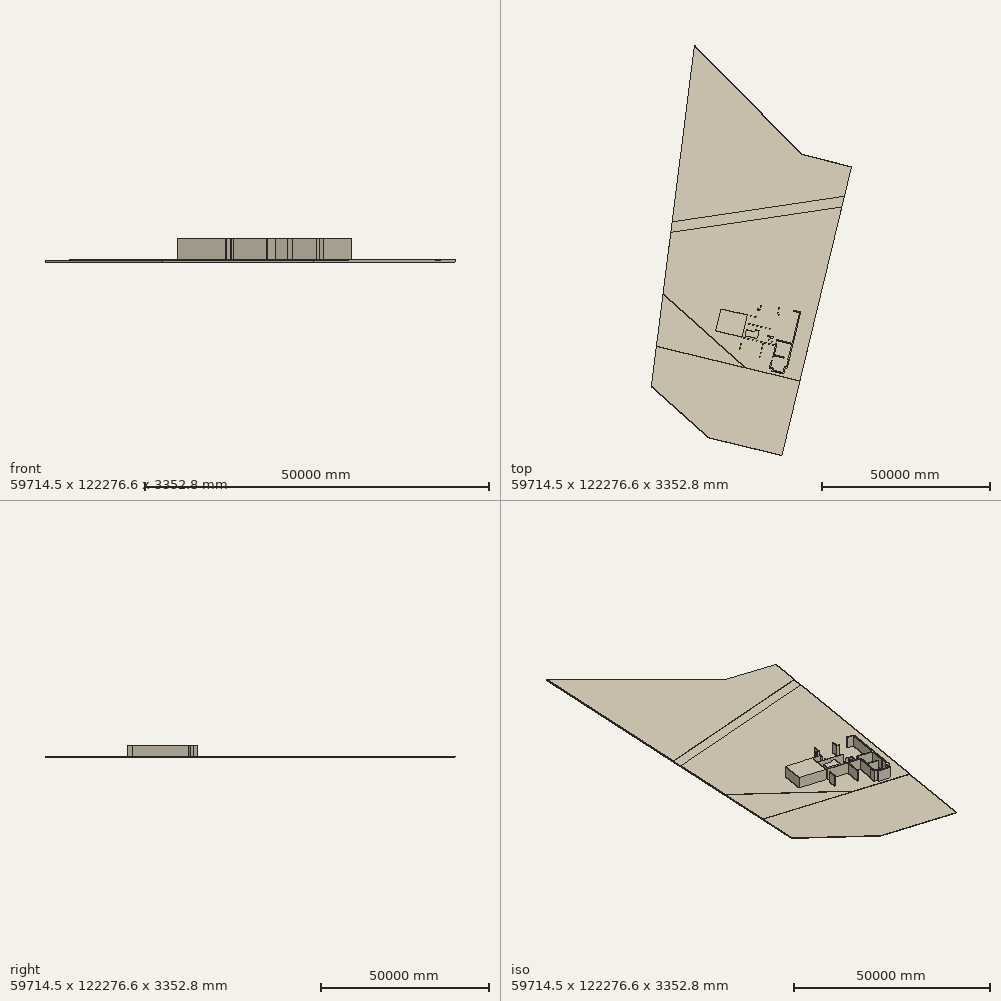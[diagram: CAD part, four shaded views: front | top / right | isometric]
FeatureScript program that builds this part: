
annotation { "Feature Type Name" : "Feature", "Feature Type Description" : "" }
export const myFeature = defineFeature(function(context is Context, id is Id, definition is map)
    precondition{}
    {
        {
            var Q0;
            Q0=qCreatedBy(makeId("Top.planeOp"),FACE);
            var sketch = newSketch(context, id + "F0", { "sketchPlane" : qUnion([Q0])});
            skLineSegment(sketch, "E0", {"start": v(0, 0) * mm, "end": v(31989.83, -32467.96) * mm});
            skLineSegment(sketch, "E1", {"start": v(31989.83, -32467.96) * mm, "end": v(46862.18, -36229.17) * mm});
            skLineSegment(sketch, "E2", {"start": v(46862.18, -36229.17) * mm, "end": v(26112.23, -122276.56) * mm});
            skLineSegment(sketch, "E3", {"start": v(46862.18, -36229.17) * mm, "end": v(46862.18, -51469.17) * mm, "construction": true});
            skLineSegment(sketch, "E4", {"start": v(0, 0) * mm, "end": v(-12852.3, -101676.89) * mm});
            skLineSegment(sketch, "E5", {"start": v(0, 0) * mm, "end": v(0, 15240) * mm, "construction": true});
            skLineSegment(sketch, "E6", {"start": v(26112.23, -122276.56) * mm, "end": v(4230, -116999.76) * mm});
            skLineSegment(sketch, "E7", {"start": v(26112.23, -122276.56) * mm, "end": v(10872.23, -122276.56) * mm, "construction": true});
            skLineSegment(sketch, "E8", {"start": v(4230, -116999.76) * mm, "end": v(-12852.3, -101676.89) * mm});
            skArc(sketch, "E9", {"start": v(-4165.07, -109469.35) * mm, "mid": v(-689.73, -114039.67) * mm, "end": v(4230, -116999.76) * mm, "construction": true});
            skArc(sketch, "E10", {"start": v(-4165.07, -109469.35) * mm, "mid": v(-8132.26, -105153.47) * mm, "end": v(-12852.3, -101676.89) * mm, "construction": true});
            skLineSegment(sketch, "E11", {"start": v(31471.2, -100053.58) * mm, "end": v(-11342.08, -89729.35) * mm});
            skLineSegment(sketch, "E12", {"start": v(-9365.85, -74095.03) * mm, "end": v(15198.72, -96129.54) * mm});
            skLineSegment(sketch, "E13", {"start": v(-6651.63, -52622.31) * mm, "end": v(44754.67, -44968.73) * mm});
            skLineSegment(sketch, "E14", {"start": v(-7048.63, -55763.02) * mm, "end": v(43983.88, -48165.09) * mm});
            skSolve(sketch);
        }
        {
            var Q0;
            {var subQ4=sQuery(id+"F0.wireOp",EDGE,"E0");Q0=makeQuery(id+"F0.imprint","IMPRINT",FACE,{"disambiguationData":[TD([[makeQuery(id+"F0.imprint","IMPRINT",EDGE,{"derivedFrom":subQ4}),-1.0]])]});}
            var Q1;
            {var subQ0=sQuery(id+"F0.wireOp",EDGE,"E13");Q1=makeQuery(id+"F0.imprint","IMPRINT",FACE,{"disambiguationData":[TD([[makeQuery(id+"F0.imprint","IMPRINT",EDGE,{"derivedFrom":subQ0}),-1.0]])]});}
            var Q2;
            {var subQ0=sQuery(id+"F0.wireOp",EDGE,"E12");Q2=makeQuery(id+"F0.imprint","IMPRINT",FACE,{"disambiguationData":[TD([[makeQuery(id+"F0.imprint","IMPRINT",EDGE,{"derivedFrom":subQ0}),1.0]])]});}
            var Q3;
            {var subQ3=sQuery(id+"F0.wireOp",EDGE,"E12");Q3=makeQuery(id+"F0.imprint","IMPRINT",FACE,{"disambiguationData":[TD([[makeQuery(id+"F0.imprint","IMPRINT",EDGE,{"derivedFrom":subQ3}),-1.0]])]});}
            var Q4;
            {var subQ1=sQuery(id+"F0.wireOp",EDGE,"E6");Q4=makeQuery(id+"F0.imprint","IMPRINT",FACE,{"disambiguationData":[TD([[makeQuery(id+"F0.imprint","IMPRINT",EDGE,{"derivedFrom":subQ1}),-1.0]])]});}
            extrude(context, id + "F1", {"entities" : qUnion([Q0, Q1, Q2, Q3, Q4]), "depth" : 304.8 * mm, "offsetDistance" : 25.4 * mm});
        }
        {
            var Q0;
            Q0=makeQuery(id+"F1.opExtrude","CAP_FACE",FACE,{"disambiguationData":[OSD([sQuery(id+"F0.wireOp",EDGE,"E0"),sQuery(id+"F0.wireOp",EDGE,"E1"),sQuery(id+"F0.wireOp",EDGE,"E2"),sQuery(id+"F0.wireOp",EDGE,"E4"),sQuery(id+"F0.wireOp",EDGE,"E6"),sQuery(id+"F0.wireOp",EDGE,"E8")])],"isStart":false});
            var sketch = newSketch(context, id + "F2", { "sketchPlane" : qUnion([Q0])});
            skLineSegment(sketch, "E15.0", {"start": v(-9365.85, -74095.03) * mm, "end": v(15198.72, -96129.54) * mm});
            skLineSegment(sketch, "E16.0", {"start": v(31471.2, -100053.58) * mm, "end": v(-11342.08, -89729.35) * mm});
            skLineSegment(sketch, "E17.0", {"start": v(0, 0) * mm, "end": v(-12852.3, -101676.89) * mm});
            skSolve(sketch);
        }
        {
            var Q0;
            {var subQ0=sQuery(id+"F2.wireOp",EDGE,"E15.0");Q0=makeQuery(id+"F2.imprint","IMPRINT",FACE,{"disambiguationData":[TD([[makeQuery(id+"F2.imprint","IMPRINT",EDGE,{"derivedFrom":subQ0}),-1.0]])]});}
            extrude(context, id + "F3", {"entities" : qUnion([Q0]), "operationType" : NewBodyOperationType.REMOVE, "oppositeDirection" : true, "depth" : 76.2 * mm, "offsetDistance" : 25.4 * mm});
        }
        {
            var Q0;
            Q0=makeQuery(id+"F1.opExtrude","CAP_FACE",FACE,{"disambiguationData":[OSD([sQuery(id+"F0.wireOp",EDGE,"E0"),sQuery(id+"F0.wireOp",EDGE,"E1"),sQuery(id+"F0.wireOp",EDGE,"E2"),sQuery(id+"F0.wireOp",EDGE,"E4"),sQuery(id+"F0.wireOp",EDGE,"E6"),sQuery(id+"F0.wireOp",EDGE,"E8")])],"isStart":false});
            var sketch = newSketch(context, id + "F4", { "sketchPlane" : qUnion([Q0])});
            skLineSegment(sketch, "E18.0", {"start": v(0, 0) * mm, "end": v(-12852.3, -101676.89) * mm});
            skLineSegment(sketch, "E19.0", {"start": v(4230, -116999.76) * mm, "end": v(-12852.3, -101676.89) * mm});
            skLineSegment(sketch, "E20.0", {"start": v(26112.23, -122276.56) * mm, "end": v(4230, -116999.76) * mm});
            skLineSegment(sketch, "E21.0", {"start": v(46862.18, -36229.17) * mm, "end": v(26112.23, -122276.56) * mm});
            skLineSegment(sketch, "E22.0", {"start": v(31471.2, -100053.58) * mm, "end": v(-11342.08, -89729.35) * mm});
            skSolve(sketch);
        }
        {
            var Q0;
            {var subQ4=sQuery(id+"F4.wireOp",EDGE,"E19.0");Q0=makeQuery(id+"F4.imprint","IMPRINT",FACE,{"disambiguationData":[TD([[makeQuery(id+"F4.imprint","IMPRINT",EDGE,{"derivedFrom":subQ4}),-1.0]])]});}
            extrude(context, id + "F5", {"entities" : qUnion([Q0]), "operationType" : NewBodyOperationType.REMOVE, "oppositeDirection" : true, "depth" : 152.4 * mm, "offsetDistance" : 25.4 * mm});
        }
        {
            var Q0;
            Q0=makeQuery(id+"F1.opExtrude","CAP_FACE",FACE,{"disambiguationData":[OSD([sQuery(id+"F0.wireOp",EDGE,"E0"),sQuery(id+"F0.wireOp",EDGE,"E1"),sQuery(id+"F0.wireOp",EDGE,"E2"),sQuery(id+"F0.wireOp",EDGE,"E4"),sQuery(id+"F0.wireOp",EDGE,"E6"),sQuery(id+"F0.wireOp",EDGE,"E8")])],"isStart":false});
            var sketch = newSketch(context, id + "F6", { "sketchPlane" : qUnion([Q0])});
            skLineSegment(sketch, "E23.0", {"start": v(-6651.63, -52622.31) * mm, "end": v(44754.67, -44968.73) * mm});
            skLineSegment(sketch, "E24.0", {"start": v(-7048.63, -55763.02) * mm, "end": v(43983.88, -48165.09) * mm});
            skLineSegment(sketch, "E25.0", {"start": v(0, 0) * mm, "end": v(-12852.3, -101676.89) * mm});
            skLineSegment(sketch, "E26.0", {"start": v(46862.18, -36229.17) * mm, "end": v(26112.23, -122276.56) * mm});
            skSolve(sketch);
        }
        {
            var Q0;
            {var subQ0=sQuery(id+"F6.wireOp",EDGE,"E23.0");Q0=makeQuery(id+"F6.imprint","IMPRINT",FACE,{"disambiguationData":[TD([[makeQuery(id+"F6.imprint","IMPRINT",EDGE,{"derivedFrom":subQ0}),-1.0]])]});}
            extrude(context, id + "F7", {"entities" : qUnion([Q0]), "operationType" : NewBodyOperationType.REMOVE, "oppositeDirection" : true, "depth" : 152.4 * mm, "offsetDistance" : 25.4 * mm});
        }
        {
            var Q0;
            {var subQ0=sQuery(id+"F0.wireOp",EDGE,"E4");var subQ1=sQuery(id+"F0.wireOp",EDGE,"E2");Q0=makeQuery(id+"F7.boolean.opBoolean","SPLIT",FACE,{"disambiguationData":[TD([makeQuery(id+"F3.boolean.opBoolean","COPY",FACE,{"derivedFrom":makeQuery(id+"F3.opExtrude","SWEPT_FACE",FACE,{"disambiguationData":[OSD([sQuery(id+"F2.wireOp",EDGE,"E15.0")])]})})])],"derivedFrom":makeQuery(id+"F1.opExtrude","CAP_FACE",FACE,{"disambiguationData":[OSD([sQuery(id+"F0.wireOp",EDGE,"E0"),sQuery(id+"F0.wireOp",EDGE,"E1"),subQ1,subQ0,sQuery(id+"F0.wireOp",EDGE,"E6"),sQuery(id+"F0.wireOp",EDGE,"E8")])],"isStart":false})});}
            var sketch = newSketch(context, id + "F8", { "sketchPlane" : qUnion([Q0])});
            skLineSegment(sketch, "E27", {"start": v(27669.68, -96315.03) * mm, "end": v(31724.64, -79499.64) * mm});
            skPoint(sketch, "E28.orphan", {"position": v(31471.2, -100053.58) * mm});
            skLineSegment(sketch, "E29", {"start": v(-5717.12, -79311.3) * mm, "end": v(3764.68, -81597.8) * mm});
            skLineSegment(sketch, "E30", {"start": v(3764.68, -81597.8) * mm, "end": v(7766.05, -65004.64) * mm});
            skLineSegment(sketch, "E31", {"start": v(7766.05, -65004.64) * mm, "end": v(-1715.76, -62718.14) * mm});
            skLineSegment(sketch, "E32", {"start": v(-1715.76, -62718.14) * mm, "end": v(-5717.12, -79311.3) * mm});
            skLineSegment(sketch, "E33", {"start": v(-5145.5, -76940.85) * mm, "end": v(-2182.44, -77655.38) * mm});
            skLineSegment(sketch, "E34", {"start": v(-2182.44, -77655.38) * mm, "end": v(-2754.06, -80025.83) * mm});
            skLineSegment(sketch, "E35", {"start": v(-5145.5, -76940.85) * mm, "end": v(-9590.1, -75869.05) * mm});
            skLineSegment(sketch, "E36", {"start": v(-2182.44, -77655.38) * mm, "end": v(1247.3, -63432.67) * mm});
            skLineSegment(sketch, "E37", {"start": v(3764.68, -81597.8) * mm, "end": v(7190.64, -82423.95) * mm});
            skLineSegment(sketch, "E38", {"start": v(4934.3, -91780.7) * mm, "end": v(-10343.91, -88096.42) * mm});
            skLineSegment(sketch, "E39.0", {"start": v(4230, -116999.76) * mm, "end": v(-12852.3, -101676.89) * mm});
            skLineSegment(sketch, "E40", {"start": v(-2047.33, -90097.1) * mm, "end": v(-6264.7, -107585.98) * mm});
            skLineSegment(sketch, "E41", {"start": v(-5603, -89239.67) * mm, "end": v(-9358.03, -104811.25) * mm});
            skArc(sketch, "E42", {"start": v(-6746.26, -93980.57) * mm, "mid": v(-7326.44, -90293.4) * mm, "end": v(-10343.91, -88096.42) * mm});
            skLineSegment(sketch, "E43", {"start": v(-8087.58, -78739.68) * mm, "end": v(-10343.91, -88096.42) * mm});
            skLineSegment(sketch, "E44", {"start": v(-5717.12, -79311.3) * mm, "end": v(-8087.58, -78739.68) * mm});
            skLineSegment(sketch, "E45", {"start": v(22775.38, -94507.71) * mm, "end": v(22346.66, -96285.55) * mm});
            skLineSegment(sketch, "E46", {"start": v(22346.66, -96285.55) * mm, "end": v(23235.58, -96499.91) * mm});
            skLineSegment(sketch, "E47", {"start": v(23235.58, -96499.91) * mm, "end": v(23092.67, -97092.52) * mm});
            skLineSegment(sketch, "E48", {"start": v(23092.67, -97092.52) * mm, "end": v(26648.35, -97949.96) * mm});
            skLineSegment(sketch, "E49", {"start": v(26648.35, -97949.96) * mm, "end": v(27077.07, -96172.12) * mm});
            skLineSegment(sketch, "E50", {"start": v(13071.34, -92167.63) * mm, "end": v(14241.39, -87315.61) * mm});
            skLineSegment(sketch, "E51", {"start": v(14241.39, -87315.61) * mm, "end": v(5985.04, -85324.63) * mm});
            skLineSegment(sketch, "E52", {"start": v(5985.04, -85324.63) * mm, "end": v(7699.91, -78213.28) * mm});
            skLineSegment(sketch, "E53", {"start": v(14020.33, -75230.32) * mm, "end": v(31724.64, -79499.64) * mm});
            skLineSegment(sketch, "E54.trimOffspring", {"start": v(27077.07, -96172.12) * mm, "end": v(27669.68, -96315.03) * mm});
            skLineSegment(sketch, "E55.0", {"start": v(6352.8, -85099.78) * mm, "end": v(7924.77, -78581.03) * mm});
            skLineSegment(sketch, "E55.1", {"start": v(23460.43, -96867.67) * mm, "end": v(26423.5, -97582.2) * mm});
            skLineSegment(sketch, "E55.2", {"start": v(26423.5, -97582.2) * mm, "end": v(26852.22, -95804.36) * mm});
            skLineSegment(sketch, "E55.3", {"start": v(26852.22, -95804.36) * mm, "end": v(27444.83, -95947.27) * mm});
            skLineSegment(sketch, "E55.4", {"start": v(27444.83, -95947.27) * mm, "end": v(28016.45, -93576.82) * mm});
            skLineSegment(sketch, "E55.5", {"start": v(23603.34, -96275.06) * mm, "end": v(23460.43, -96867.67) * mm});
            skLineSegment(sketch, "E55.6", {"start": v(14245.18, -75598.08) * mm, "end": v(19282.4, -76812.78) * mm});
            skLineSegment(sketch, "E55.7", {"start": v(22714.42, -96060.7) * mm, "end": v(23603.34, -96275.06) * mm});
            skLineSegment(sketch, "E55.8", {"start": v(23143.14, -94282.86) * mm, "end": v(22714.42, -96060.7) * mm});
            skLineSegment(sketch, "E55.9", {"start": v(13439.1, -91942.77) * mm, "end": v(23143.14, -94282.86) * mm});
            skLineSegment(sketch, "E55.10", {"start": v(13439.1, -91942.77) * mm, "end": v(14609.14, -87090.76) * mm});
            skLineSegment(sketch, "E55.11", {"start": v(14609.14, -87090.76) * mm, "end": v(6352.8, -85099.78) * mm});
            skLineSegment(sketch, "E56", {"start": v(14609.14, -87090.76) * mm, "end": v(19350.05, -88234) * mm});
            skLineSegment(sketch, "E57", {"start": v(20619.6, -88657.73) * mm, "end": v(19476.35, -93398.63) * mm});
            skLineSegment(sketch, "E58.0", {"start": v(20508.48, -88630.93) * mm, "end": v(19365.23, -93371.83) * mm});
            skLineSegment(sketch, "E58.1", {"start": v(14582.35, -87201.87) * mm, "end": v(20508.48, -88630.93) * mm});
            skLineSegment(sketch, "E59", {"start": v(17710.43, -83331.52) * mm, "end": v(18255.26, -81072.19) * mm});
            skLineSegment(sketch, "E60", {"start": v(17821.54, -83358.32) * mm, "end": v(19393.5, -76839.58) * mm});
            skLineSegment(sketch, "E61", {"start": v(7924.77, -78581.03) * mm, "end": v(18255.26, -81072.19) * mm});
            skLineSegment(sketch, "E62", {"start": v(14020.33, -75230.32) * mm, "end": v(12993.2, -79489.73) * mm});
            skLineSegment(sketch, "E63", {"start": v(12993.2, -79489.73) * mm, "end": v(7699.91, -78213.28) * mm});
            skLineSegment(sketch, "E64", {"start": v(14245.18, -75598.08) * mm, "end": v(13218.05, -79857.49) * mm});
            skLineSegment(sketch, "E65", {"start": v(13244.84, -79746.37) * mm, "end": v(18282.05, -80961.07) * mm});
            skLineSegment(sketch, "E66", {"start": v(23143.14, -94282.86) * mm, "end": v(23571.86, -92505.02) * mm});
            skLineSegment(sketch, "E67", {"start": v(24202.07, -89404.05) * mm, "end": v(19350.05, -88234) * mm});
            skLineSegment(sketch, "E68", {"start": v(23032.02, -94256.07) * mm, "end": v(24175.27, -89515.16) * mm});
            skLineSegment(sketch, "E69", {"start": v(24175.27, -89515.16) * mm, "end": v(20619.6, -88657.73) * mm});
            skLineSegment(sketch, "E70", {"start": v(19833.61, -91917.1) * mm, "end": v(21018.84, -92202.9) * mm});
            skLineSegment(sketch, "E71", {"start": v(21018.84, -92202.9) * mm, "end": v(21519, -90128.76) * mm});
            skLineSegment(sketch, "E72", {"start": v(21519, -90128.76) * mm, "end": v(23889.46, -90700.39) * mm});
            skLineSegment(sketch, "E73", {"start": v(23571.86, -92505.02) * mm, "end": v(28016.45, -93576.82) * mm});
            skLineSegment(sketch, "E74", {"start": v(23828.5, -92253.37) * mm, "end": v(27982.96, -93255.2) * mm});
            skLineSegment(sketch, "E75.trimOffspring", {"start": v(18282.05, -80961.07) * mm, "end": v(19282.4, -76812.78) * mm});
            skLineSegment(sketch, "E76", {"start": v(28983.3, -89106.91) * mm, "end": v(24828.84, -88105.08) * mm});
            skLineSegment(sketch, "E77", {"start": v(27982.96, -93255.2) * mm, "end": v(28983.3, -89106.91) * mm});
            skLineSegment(sketch, "E78", {"start": v(23828.5, -92253.37) * mm, "end": v(24828.84, -88105.08) * mm});
            skLineSegment(sketch, "E79.trimOffspring", {"start": v(29159.7, -88835.91) * mm, "end": v(31356.88, -79724.5) * mm});
            skLineSegment(sketch, "E80", {"start": v(29159.7, -88835.91) * mm, "end": v(24603.99, -87737.32) * mm});
            skLineSegment(sketch, "E81", {"start": v(24603.99, -87737.32) * mm, "end": v(24202.07, -89404.05) * mm});
            skLineSegment(sketch, "E82", {"start": v(26023.36, -78438.34) * mm, "end": v(24951.57, -82882.93) * mm});
            skLineSegment(sketch, "E83", {"start": v(24951.57, -82882.93) * mm, "end": v(30285.09, -84169.09) * mm});
            skLineSegment(sketch, "E84", {"start": v(25912.25, -78411.54) * mm, "end": v(24340.28, -84930.28) * mm});
            skLineSegment(sketch, "E85", {"start": v(24924.77, -82994.05) * mm, "end": v(30258.3, -84280.2) * mm});
            skLineSegment(sketch, "E86", {"start": v(21057.5, -78390.48) * mm, "end": v(23724.26, -79033.55) * mm});
            skLineSegment(sketch, "E87", {"start": v(23724.26, -79033.55) * mm, "end": v(23474.18, -80070.63) * mm});
            skLineSegment(sketch, "E88", {"start": v(23474.18, -80070.63) * mm, "end": v(20807.42, -79427.55) * mm});
            skLineSegment(sketch, "E89", {"start": v(20807.42, -79427.55) * mm, "end": v(21057.5, -78390.48) * mm});
            skLineSegment(sketch, "E90", {"start": v(12993.2, -79489.73) * mm, "end": v(12921.74, -79786.03) * mm});
            skLineSegment(sketch, "E91", {"start": v(17821.54, -83358.32) * mm, "end": v(24340.28, -84930.28) * mm});
            skLineSegment(sketch, "E92", {"start": v(25961.85, -83244.13) * mm, "end": v(25553.97, -84935.55) * mm});
            skLineSegment(sketch, "E93", {"start": v(15313.18, -82871.01) * mm, "end": v(24424.6, -85068.2) * mm});
            skLineSegment(sketch, "E94", {"start": v(24424.6, -85068.2) * mm, "end": v(24924.77, -82994.05) * mm});
            skLineSegment(sketch, "E95", {"start": v(25054.81, -81967.22) * mm, "end": v(24462.2, -81824.31) * mm});
            skLineSegment(sketch, "E96", {"start": v(24462.2, -81824.31) * mm, "end": v(23747.67, -84787.38) * mm});
            skLineSegment(sketch, "E97", {"start": v(22853.5, -83944.68) * mm, "end": v(17964.45, -82765.7) * mm});
            skLineSegment(sketch, "E98", {"start": v(18807.15, -81871.54) * mm, "end": v(19128.68, -80538.16) * mm});
            skLineSegment(sketch, "E99", {"start": v(19128.68, -80538.16) * mm, "end": v(18536.07, -80395.25) * mm});
            skLineSegment(sketch, "E100", {"start": v(20165.76, -80788.24) * mm, "end": v(19879.94, -81973.47) * mm});
            skLineSegment(sketch, "E101", {"start": v(19879.94, -81973.47) * mm, "end": v(23139.32, -82759.45) * mm});
            skLineSegment(sketch, "E102", {"start": v(23139.32, -82759.45) * mm, "end": v(23425.13, -81574.23) * mm});
            skLineSegment(sketch, "E103", {"start": v(23425.13, -81574.23) * mm, "end": v(20165.76, -80788.24) * mm});
            skLineSegment(sketch, "E104", {"start": v(18920.13, -78802.6) * mm, "end": v(19512.74, -78945.51) * mm});
            skLineSegment(sketch, "E105", {"start": v(19512.74, -78945.51) * mm, "end": v(19986.12, -76982.48) * mm});
            skLineSegment(sketch, "E106.0", {"start": v(19597.06, -79083.42) * mm, "end": v(20097.24, -77009.28) * mm});
            skLineSegment(sketch, "E106.1", {"start": v(18893.34, -78913.72) * mm, "end": v(19597.06, -79083.42) * mm});
            skLineSegment(sketch, "E107", {"start": v(19393.5, -76839.58) * mm, "end": v(25912.25, -78411.54) * mm});
            skLineSegment(sketch, "E108.trimOffspring", {"start": v(26023.36, -78438.34) * mm, "end": v(31356.88, -79724.5) * mm});
            skLineSegment(sketch, "E109", {"start": v(27837.43, -93533.65) * mm, "end": v(27908.89, -93237.34) * mm});
            skLineSegment(sketch, "E110", {"start": v(26948.51, -93319.29) * mm, "end": v(27019.97, -93022.98) * mm});
            skLineSegment(sketch, "E111", {"start": v(26972.33, -93220.52) * mm, "end": v(27861.25, -93434.88) * mm});
            skLineSegment(sketch, "E112", {"start": v(26963.4, -93257.56) * mm, "end": v(27852.32, -93471.92) * mm});
            skLineSegment(sketch, "E113", {"start": v(24810.98, -88179.16) * mm, "end": v(24514.67, -88107.7) * mm});
            skLineSegment(sketch, "E114", {"start": v(24300.31, -88996.63) * mm, "end": v(24596.62, -89068.08) * mm});
            skLineSegment(sketch, "E115", {"start": v(24362.04, -89011.51) * mm, "end": v(24576.4, -88122.6) * mm});
            skLineSegment(sketch, "E116", {"start": v(24399.08, -89020.44) * mm, "end": v(24613.44, -88131.52) * mm});
            skLineSegment(sketch, "E117", {"start": v(23016.84, -89118.24) * mm, "end": v(23543.8, -86932.98) * mm});
            skLineSegment(sketch, "E118", {"start": v(22905.73, -89091.44) * mm, "end": v(23405.9, -87017.3) * mm});
            skLineSegment(sketch, "E119", {"start": v(15884.8, -80500.56) * mm, "end": v(14312.84, -87019.3) * mm});
            skLineSegment(sketch, "E120", {"start": v(15339.97, -82759.9) * mm, "end": v(17710.43, -83331.52) * mm});
            skLineSegment(sketch, "E121", {"start": v(18807.15, -81871.54) * mm, "end": v(18214.53, -81728.63) * mm});
            skLineSegment(sketch, "E122", {"start": v(13071.34, -92167.63) * mm, "end": v(23071.68, -94579.17) * mm});
            skLineSegment(sketch, "E123", {"start": v(19247.36, -85896.9) * mm, "end": v(23543.8, -86932.98) * mm});
            skLineSegment(sketch, "E124", {"start": v(19109.45, -85981.23) * mm, "end": v(19739.1, -86133.06) * mm});
            skLineSegment(sketch, "E125", {"start": v(22016.8, -88877.08) * mm, "end": v(22516.98, -86802.94) * mm});
            skLineSegment(sketch, "E126", {"start": v(21905.7, -88850.29) * mm, "end": v(22405.86, -86776.14) * mm});
            skLineSegment(sketch, "E127", {"start": v(20090.81, -88412.64) * mm, "end": v(20590.98, -86338.5) * mm});
            skLineSegment(sketch, "E128", {"start": v(20201.93, -88439.43) * mm, "end": v(20702.1, -86365.29) * mm});
            skLineSegment(sketch, "E129", {"start": v(20344.83, -87846.82) * mm, "end": v(22048.6, -88257.67) * mm});
            skCircle(sketch, "E130", {"center": v(20717.84, -88250.3) * mm, "radius": 152.4 * mm});
            skCircle(sketch, "E131", {"center": v(21532.68, -88446.8) * mm, "radius": 152.4 * mm});
            skLineSegment(sketch, "E132", {"start": v(19473.5, -88263.78) * mm, "end": v(19544.96, -87967.47) * mm});
            skLineSegment(sketch, "E133", {"start": v(19544.96, -87967.47) * mm, "end": v(20038.8, -88086.56) * mm});
            skLineSegment(sketch, "E134", {"start": v(20038.8, -88086.56) * mm, "end": v(19967.35, -88382.87) * mm});
            skLineSegment(sketch, "E135", {"start": v(19643.73, -87991.29) * mm, "end": v(19756.86, -87522.14) * mm});
            skLineSegment(sketch, "E136", {"start": v(19756.86, -87522.14) * mm, "end": v(20053.17, -87593.59) * mm});
            skLineSegment(sketch, "E137", {"start": v(20053.17, -87593.59) * mm, "end": v(19940.04, -88062.74) * mm});
            skLineSegment(sketch, "E138", {"start": v(19760.9, -86530.24) * mm, "end": v(20501.67, -86708.88) * mm});
            skLineSegment(sketch, "E139", {"start": v(20600.87, -86785.05) * mm, "end": v(20489.76, -86758.26) * mm});
            skLineSegment(sketch, "E140", {"start": v(20346.85, -87350.87) * mm, "end": v(20457.97, -87377.67) * mm});
            skLineSegment(sketch, "E141", {"start": v(20402.41, -87364.27) * mm, "end": v(20545.32, -86771.66) * mm});
            skArc(sketch, "E142", {"start": v(20402.41, -87364.27) * mm, "mid": v(20012.42, -87067.68) * mm, "end": v(19966.67, -86579.86) * mm, "construction": true});
            skLineSegment(sketch, "E143", {"start": v(22231.16, -87988.16) * mm, "end": v(23120.08, -88202.52) * mm});
            skLineSegment(sketch, "E144", {"start": v(23120.08, -88202.52) * mm, "end": v(22016.8, -88877.08) * mm});
            skLineSegment(sketch, "E145", {"start": v(22231.16, -87988.16) * mm, "end": v(22905.73, -89091.44) * mm});
            skCircle(sketch, "E146", {"center": v(22568.44, -88539.8) * mm, "radius": 50.8 * mm});
            skLineSegment(sketch, "E147", {"start": v(22427.66, -87173.32) * mm, "end": v(23316.58, -87387.68) * mm});
            skLineSegment(sketch, "E148", {"start": v(22304.64, -87195.9) * mm, "end": v(22415.75, -87222.7) * mm});
            skLineSegment(sketch, "E149", {"start": v(22161.73, -87788.52) * mm, "end": v(22272.85, -87815.32) * mm});
            skLineSegment(sketch, "E150", {"start": v(22360.2, -87209.3) * mm, "end": v(22217.29, -87801.92) * mm});
            skArc(sketch, "E151", {"start": v(22217.29, -87801.92) * mm, "mid": v(22699.6, -87715.68) * mm, "end": v(22962.65, -87302.33) * mm, "construction": true});
            skLineSegment(sketch, "E152", {"start": v(19461.72, -85007.99) * mm, "end": v(21239.56, -85436.7) * mm});
            skLineSegment(sketch, "E153", {"start": v(19390.27, -85304.3) * mm, "end": v(21168.1, -85733.01) * mm});
            skLineSegment(sketch, "E154", {"start": v(20612.78, -86735.67) * mm, "end": v(20909.09, -86807.12) * mm});
            skLineSegment(sketch, "E155", {"start": v(21239.56, -85436.7) * mm, "end": v(21025.2, -86325.63) * mm});
            skLineSegment(sketch, "E156", {"start": v(21980.33, -85615.34) * mm, "end": v(21765.97, -86504.26) * mm});
            skLineSegment(sketch, "E157", {"start": v(21099.28, -86343.49) * mm, "end": v(21072.48, -86454.6) * mm});
            skLineSegment(sketch, "E158", {"start": v(21691.9, -86486.4) * mm, "end": v(21665.1, -86597.5) * mm});
            skLineSegment(sketch, "E159", {"start": v(21085.88, -86399.05) * mm, "end": v(21678.5, -86541.95) * mm});
            skLineSegment(sketch, "E160", {"start": v(20909.09, -86807.12) * mm, "end": v(20998.4, -86436.74) * mm});
            skLineSegment(sketch, "E161", {"start": v(21649.86, -86985.76) * mm, "end": v(21739.17, -86615.37) * mm});
            skLineSegment(sketch, "E162.trimOffspring", {"start": v(21649.86, -86985.76) * mm, "end": v(22316.55, -87146.52) * mm});
            skLineSegment(sketch, "E163.trimOffspring", {"start": v(21908.87, -85911.64) * mm, "end": v(23686.71, -86340.36) * mm});
            skLineSegment(sketch, "E164.trimOffspring", {"start": v(21980.33, -85615.34) * mm, "end": v(23758.16, -86044.06) * mm});
            skLineSegment(sketch, "E165", {"start": v(15482.88, -82167.29) * mm, "end": v(17853.33, -82738.9) * mm});
            skLineSegment(sketch, "E166", {"start": v(15741.9, -81093.17) * mm, "end": v(18112.35, -81664.8) * mm});
            skLineSegment(sketch, "E167", {"start": v(17889.06, -82590.76) * mm, "end": v(18000.17, -82617.55) * mm});
            skLineSegment(sketch, "E168", {"start": v(18067.7, -81850) * mm, "end": v(18178.8, -81876.79) * mm});
            skLineSegment(sketch, "E169", {"start": v(18123.25, -81863.39) * mm, "end": v(17944.62, -82604.15) * mm});
            skLineSegment(sketch, "E170", {"start": v(15397.07, -82035.55) * mm, "end": v(15508.19, -82062.34) * mm});
            skLineSegment(sketch, "E171", {"start": v(15611.43, -81146.63) * mm, "end": v(15722.55, -81173.42) * mm});
            skLineSegment(sketch, "E172", {"start": v(15666.99, -81160.03) * mm, "end": v(15452.63, -82048.95) * mm});
            skLineSegment(sketch, "E173", {"start": v(22853.5, -83944.68) * mm, "end": v(22710.6, -84537.3) * mm});
            skLineSegment(sketch, "E174", {"start": v(22784.67, -84555.16) * mm, "end": v(22757.88, -84666.27) * mm});
            skLineSegment(sketch, "E175", {"start": v(23673.6, -84769.51) * mm, "end": v(23646.8, -84880.63) * mm});
            skLineSegment(sketch, "E176", {"start": v(25412.08, -80485.69) * mm, "end": v(24708.35, -80315.99) * mm});
            skLineSegment(sketch, "E177", {"start": v(24708.35, -80315.99) * mm, "end": v(25208.52, -78241.84) * mm});
            skLineSegment(sketch, "E178", {"start": v(18460.68, -80220.3) * mm, "end": v(18571.8, -80247.1) * mm});
            skLineSegment(sketch, "E179", {"start": v(18746.5, -79035.08) * mm, "end": v(18857.6, -79061.87) * mm});
            skLineSegment(sketch, "E180", {"start": v(19210.94, -77109.09) * mm, "end": v(19322.05, -77135.88) * mm});
            skLineSegment(sketch, "E181", {"start": v(18877.5, -78491.85) * mm, "end": v(18988.6, -78518.65) * mm});
            skLineSegment(sketch, "E182", {"start": v(19044.22, -77800.47) * mm, "end": v(19155.33, -77827.26) * mm});
            skLineSegment(sketch, "E183", {"start": v(18933.05, -78505.25) * mm, "end": v(19099.77, -77813.87) * mm});
            skLineSegment(sketch, "E184", {"start": v(19099.77, -77813.87) * mm, "end": v(19266.5, -77122.48) * mm});
            skLineSegment(sketch, "E185", {"start": v(25319.64, -78268.64) * mm, "end": v(24846.26, -80231.67) * mm});
            skLineSegment(sketch, "E186", {"start": v(24846.26, -80231.67) * mm, "end": v(25438.87, -80374.57) * mm});
            skLineSegment(sketch, "E187", {"start": v(26072.96, -83270.93) * mm, "end": v(25665.08, -84962.34) * mm});
            skLineSegment(sketch, "E188", {"start": v(25715.7, -84752.46) * mm, "end": v(29901.03, -85761.73) * mm});
            skLineSegment(sketch, "E189", {"start": v(25688.9, -84863.58) * mm, "end": v(29874.23, -85872.85) * mm});
            skLineSegment(sketch, "E190", {"start": v(28554.53, -83869.35) * mm, "end": v(28197.26, -85350.88) * mm});
            skLineSegment(sketch, "E191", {"start": v(28443.41, -83842.55) * mm, "end": v(28086.15, -85324.08) * mm});
            skLineSegment(sketch, "E192", {"start": v(27702.65, -83663.92) * mm, "end": v(27345.38, -85145.45) * mm});
            skLineSegment(sketch, "E193", {"start": v(25941.96, -83814.16) * mm, "end": v(26830.88, -84028.52) * mm});
            skLineSegment(sketch, "E194", {"start": v(26830.88, -84028.52) * mm, "end": v(26961.88, -83485.29) * mm});
            skLineSegment(sketch, "E195", {"start": v(27085.34, -83515.06) * mm, "end": v(27013.89, -83811.37) * mm});
            skLineSegment(sketch, "E196", {"start": v(27013.89, -83811.37) * mm, "end": v(27507.73, -83930.45) * mm});
            skLineSegment(sketch, "E197", {"start": v(27507.73, -83930.45) * mm, "end": v(27579.19, -83634.15) * mm});
            skLineSegment(sketch, "E198", {"start": v(27112.66, -83835.18) * mm, "end": v(26999.52, -84304.34) * mm});
            skLineSegment(sketch, "E199", {"start": v(26999.52, -84304.34) * mm, "end": v(27295.83, -84375.79) * mm});
            skLineSegment(sketch, "E200", {"start": v(27295.83, -84375.79) * mm, "end": v(27408.96, -83906.64) * mm});
            skLineSegment(sketch, "E201", {"start": v(25762.98, -84881.44) * mm, "end": v(25789.77, -84770.32) * mm});
            skLineSegment(sketch, "E202", {"start": v(26355.6, -85024.34) * mm, "end": v(26382.39, -84913.23) * mm});
            skLineSegment(sketch, "E203", {"start": v(25776.38, -84825.88) * mm, "end": v(26368.99, -84968.79) * mm});
            skArc(sketch, "E204", {"start": v(26368.99, -84968.79) * mm, "mid": v(26275.53, -84475.95) * mm, "end": v(25844.08, -84220.05) * mm, "construction": true});
            skLineSegment(sketch, "E205", {"start": v(28340.17, -84758.27) * mm, "end": v(30043.93, -85169.12) * mm});
            skLineSegment(sketch, "E206", {"start": v(28366.96, -84647.15) * mm, "end": v(30070.73, -85058) * mm});
            skLineSegment(sketch, "E207", {"start": v(29278.79, -88342.07) * mm, "end": v(27303.41, -87865.72) * mm});
            skLineSegment(sketch, "E208", {"start": v(27303.41, -87865.72) * mm, "end": v(27755.95, -85989.1) * mm});
            skLineSegment(sketch, "E209", {"start": v(27755.95, -85989.1) * mm, "end": v(29731.32, -86465.46) * mm});
            skLineSegment(sketch, "E210", {"start": v(28296.03, -85374.7) * mm, "end": v(28269.24, -85485.81) * mm});
            skLineSegment(sketch, "E211", {"start": v(29777.56, -85731.96) * mm, "end": v(29750.77, -85843.08) * mm});
            skLineSegment(sketch, "E212", {"start": v(29036.8, -85553.33) * mm, "end": v(29010, -85664.44) * mm});
            skLineSegment(sketch, "E213", {"start": v(28282.63, -85430.25) * mm, "end": v(29023.4, -85608.89) * mm});
            skLineSegment(sketch, "E214", {"start": v(29023.4, -85608.89) * mm, "end": v(29764.17, -85787.52) * mm});
            skArc(sketch, "E215", {"start": v(25137.16, -86664) * mm, "mid": v(24733.67, -87037.01) * mm, "end": v(24922.8, -87552.92) * mm});
            skLineSegment(sketch, "E216", {"start": v(26429.67, -85042.2) * mm, "end": v(26197.45, -86005.2) * mm});
            skLineSegment(sketch, "E217", {"start": v(26197.45, -86005.2) * mm, "end": v(25456.68, -85826.57) * mm});
            skLineSegment(sketch, "E218", {"start": v(26540.78, -85069) * mm, "end": v(26281.77, -86143.11) * mm});
            skLineSegment(sketch, "E219", {"start": v(26281.77, -86143.11) * mm, "end": v(25429.88, -85937.69) * mm});
            skLineSegment(sketch, "E220", {"start": v(26405.85, -85140.98) * mm, "end": v(26516.97, -85167.77) * mm});
            skLineSegment(sketch, "E221", {"start": v(26215.3, -85931.13) * mm, "end": v(26326.42, -85957.92) * mm});
            skLineSegment(sketch, "E222", {"start": v(26461.4, -85154.37) * mm, "end": v(26270.87, -85944.52) * mm});
            skArc(sketch, "E223", {"start": v(26270.87, -85944.52) * mm, "mid": v(26927.99, -85819.92) * mm, "end": v(27269.18, -85244.65) * mm, "construction": true});
            skLineSegment(sketch, "E224", {"start": v(25363.43, -85725.7) * mm, "end": v(25474.54, -85752.5) * mm});
            skLineSegment(sketch, "E225", {"start": v(25553.97, -84935.55) * mm, "end": v(25665.08, -84962.34) * mm});
            skLineSegment(sketch, "E226.trimOffspring", {"start": v(25363.43, -85725.7) * mm, "end": v(24863.26, -87799.85) * mm});
            skLineSegment(sketch, "E227.trimOffspring", {"start": v(25474.54, -85752.5) * mm, "end": v(24974.37, -87826.64) * mm});
            skLineSegment(sketch, "E228", {"start": v(24733.67, -87037.01) * mm, "end": v(25029.98, -87108.46) * mm, "construction": true});
            skLineSegment(sketch, "E229", {"start": v(23543.8, -86932.98) * mm, "end": v(23758.16, -86044.06) * mm});
            skLineSegment(sketch, "E230", {"start": v(20717.84, -88250.3) * mm, "end": v(21532.68, -88446.8) * mm, "construction": true});
            skLineSegment(sketch, "E231", {"start": v(14201.72, -86992.5) * mm, "end": v(15773.69, -80473.77) * mm});
            skLineSegment(sketch, "E232", {"start": v(15063.1, -83908.09) * mm, "end": v(19470.65, -84970.95) * mm});
            skLineSegment(sketch, "E233", {"start": v(19739.1, -86133.06) * mm, "end": v(19238.93, -88207.2) * mm});
            skLineSegment(sketch, "E234", {"start": v(19470.65, -84970.95) * mm, "end": v(19247.36, -85896.9) * mm});
            skLineSegment(sketch, "E235.trimOffspring", {"start": v(19850.22, -86159.86) * mm, "end": v(19350.05, -88234) * mm});
            skLineSegment(sketch, "E236.trimOffspring", {"start": v(19850.22, -86159.86) * mm, "end": v(23405.9, -87017.3) * mm});
            skLineSegment(sketch, "E237", {"start": v(15036.3, -84019.2) * mm, "end": v(19332.74, -85055.27) * mm});
            skLineSegment(sketch, "E238", {"start": v(19332.74, -85055.27) * mm, "end": v(19109.45, -85981.23) * mm});
            skLineSegment(sketch, "E239", {"start": v(23000.54, -90486.03) * mm, "end": v(23286.35, -89300.8) * mm});
            skLineSegment(sketch, "E240", {"start": v(20809.72, -93720.17) * mm, "end": v(20738.27, -94016.47) * mm});
            skLineSegment(sketch, "E241", {"start": v(21698.64, -93934.53) * mm, "end": v(21627.2, -94230.83) * mm});
            skLineSegment(sketch, "E242", {"start": v(20774, -93868.32) * mm, "end": v(21662.92, -94082.68) * mm});
            skLineSegment(sketch, "E243", {"start": v(18295.67, -84805.18) * mm, "end": v(18152.76, -85397.8) * mm});
            skLineSegment(sketch, "E244", {"start": v(18152.76, -85397.8) * mm, "end": v(15486, -84754.72) * mm});
            skLineSegment(sketch, "E245", {"start": v(15486, -84754.72) * mm, "end": v(15048.36, -86569.6) * mm});
            skLineSegment(sketch, "E246", {"start": v(15048.36, -86569.6) * mm, "end": v(18789.23, -87471.7) * mm});
            skLineSegment(sketch, "E247", {"start": v(18789.23, -87471.7) * mm, "end": v(19146.5, -85990.16) * mm});
            skLineSegment(sketch, "E248", {"start": v(18396.54, -84711.93) * mm, "end": v(18369.75, -84823.05) * mm});
            skLineSegment(sketch, "E249", {"start": v(19285.46, -84926.3) * mm, "end": v(19258.67, -85037.4) * mm});
            skLineSegment(sketch, "E250", {"start": v(18383.14, -84767.49) * mm, "end": v(19272.06, -84981.85) * mm});
            skArc(sketch, "E251", {"start": v(18383.14, -84767.49) * mm, "mid": v(18512.5, -85490.95) * mm, "end": v(19132.53, -85885.54) * mm, "construction": true});
            skArc(sketch, "E252", {"start": v(24399.08, -89020.44) * mm, "mid": v(25122.55, -88891.09) * mm, "end": v(25517.13, -88271.06) * mm, "construction": true});
            skArc(sketch, "E253", {"start": v(26972.33, -93220.52) * mm, "mid": v(27417.21, -92635.53) * mm, "end": v(28148.94, -92566.91) * mm, "construction": true});
            skArc(sketch, "E254", {"start": v(21678.5, -86541.95) * mm, "mid": v(21370.68, -86938.03) * mm, "end": v(20870.02, -86969.15) * mm, "construction": true});
            skLineSegment(sketch, "E255", {"start": v(28435.5, -91378.6) * mm, "end": v(27052.74, -91045.15) * mm});
            skLineSegment(sketch, "E256", {"start": v(26412.84, -90773.26) * mm, "end": v(25933.51, -92760.99) * mm});
            skLineSegment(sketch, "E257", {"start": v(25822.4, -92734.2) * mm, "end": v(26301.73, -90746.47) * mm});
            skLineSegment(sketch, "E258", {"start": v(27079.53, -90934.03) * mm, "end": v(28462.3, -91267.48) * mm});
            skLineSegment(sketch, "E259", {"start": v(27872.16, -88838.96) * mm, "end": v(27401.76, -90789.65) * mm});
            skLineSegment(sketch, "E260", {"start": v(27401.76, -90789.65) * mm, "end": v(28512.9, -91057.6) * mm});
            skLineSegment(sketch, "E261", {"start": v(27694.73, -91199.96) * mm, "end": v(27444.65, -92237.04) * mm});
            skLineSegment(sketch, "E262", {"start": v(27444.65, -92237.04) * mm, "end": v(27987.88, -92368.03) * mm});
            skLineSegment(sketch, "E263", {"start": v(27987.88, -92368.03) * mm, "end": v(28237.96, -91330.96) * mm});
            skLineSegment(sketch, "E264", {"start": v(27798.08, -88821.1) * mm, "end": v(27530.13, -89932.25) * mm});
            skLineSegment(sketch, "E265", {"start": v(27530.13, -89932.25) * mm, "end": v(25579.45, -89461.85) * mm});
            skLineSegment(sketch, "E266", {"start": v(25579.45, -89461.85) * mm, "end": v(25847.4, -88350.7) * mm});
            skLineSegment(sketch, "E267", {"start": v(27497.2, -91152.33) * mm, "end": v(27306.65, -91942.48) * mm});
            skLineSegment(sketch, "E268", {"start": v(27306.65, -91942.48) * mm, "end": v(26936.27, -91853.16) * mm});
            skLineSegment(sketch, "E269", {"start": v(26936.27, -91853.16) * mm, "end": v(27126.81, -91063.01) * mm});
            skLineSegment(sketch, "E270", {"start": v(24281.04, -90376.77) * mm, "end": v(26256.41, -90853.12) * mm});
            skLineSegment(sketch, "E271", {"start": v(26256.41, -90853.12) * mm, "end": v(25803.88, -92729.73) * mm});
            skLineSegment(sketch, "E272", {"start": v(27079.53, -90934.03) * mm, "end": v(27052.74, -91045.15) * mm});
            skLineSegment(sketch, "E273", {"start": v(26301.73, -90746.47) * mm, "end": v(26412.84, -90773.26) * mm});
            skLineSegment(sketch, "E274", {"start": v(13369.06, -90933.02) * mm, "end": v(13665.37, -91004.47) * mm});
            skLineSegment(sketch, "E275", {"start": v(14012.14, -88266.26) * mm, "end": v(14308.45, -88337.71) * mm});
            skLineSegment(sketch, "E276", {"start": v(14160.3, -88301.99) * mm, "end": v(13517.22, -90968.74) * mm});
            skLineSegment(sketch, "E277", {"start": v(30171.65, -79438.68) * mm, "end": v(31071.07, -80909.72) * mm});
            skLineSegment(sketch, "E278", {"start": v(30928.16, -81502.33) * mm, "end": v(30236.78, -81335.6) * mm});
            skLineSegment(sketch, "E279", {"start": v(30236.78, -81335.6) * mm, "end": v(29879.52, -82817.14) * mm});
            skLineSegment(sketch, "E280", {"start": v(29879.52, -82817.14) * mm, "end": v(30570.9, -82983.86) * mm});
            skLineSegment(sketch, "E281", {"start": v(25090.54, -81819.07) * mm, "end": v(25201.65, -81845.86) * mm});
            skLineSegment(sketch, "E282", {"start": v(25376.35, -80633.84) * mm, "end": v(25487.47, -80660.63) * mm});
            skLineSegment(sketch, "E283", {"start": v(24998.85, -83011.91) * mm, "end": v(25025.65, -82900.8) * mm});
            skLineSegment(sketch, "E284", {"start": v(25887.77, -83226.27) * mm, "end": v(25914.57, -83115.16) * mm});
            skLineSegment(sketch, "E285", {"start": v(25012.25, -82956.35) * mm, "end": v(25901.17, -83170.71) * mm});
            skArc(sketch, "E286", {"start": v(25901.17, -83170.71) * mm, "mid": v(25771.81, -82447.25) * mm, "end": v(25151.79, -82052.66) * mm, "construction": true});
            skLineSegment(sketch, "E287", {"start": v(28653.3, -83893.16) * mm, "end": v(28680.1, -83782.05) * mm});
            skLineSegment(sketch, "E288", {"start": v(29420.86, -83960.68) * mm, "end": v(29394.06, -84071.8) * mm});
            skLineSegment(sketch, "E289", {"start": v(30161.62, -84139.31) * mm, "end": v(30134.83, -84250.43) * mm});
            skLineSegment(sketch, "E290", {"start": v(28666.7, -83837.6) * mm, "end": v(29407.46, -84016.24) * mm});
            skLineSegment(sketch, "E291", {"start": v(29407.46, -84016.24) * mm, "end": v(30148.23, -84194.87) * mm});
            skLineSegment(sketch, "E292", {"start": v(26761.5, -78302.8) * mm, "end": v(26690.05, -78599.1) * mm});
            skLineSegment(sketch, "E293", {"start": v(27502.27, -78481.43) * mm, "end": v(27430.82, -78777.74) * mm});
            skLineSegment(sketch, "E294", {"start": v(27798.58, -78552.88) * mm, "end": v(27727.13, -78849.2) * mm});
            skLineSegment(sketch, "E295", {"start": v(28539.35, -78731.52) * mm, "end": v(28467.9, -79027.82) * mm});
            skLineSegment(sketch, "E296", {"start": v(28835.65, -78802.97) * mm, "end": v(28764.2, -79099.28) * mm});
            skLineSegment(sketch, "E297", {"start": v(29576.42, -78981.6) * mm, "end": v(29504.96, -79277.9) * mm});
            skLineSegment(sketch, "E298", {"start": v(27466.55, -78629.58) * mm, "end": v(26725.78, -78450.95) * mm});
            skLineSegment(sketch, "E299", {"start": v(27762.85, -78701.04) * mm, "end": v(28503.62, -78879.67) * mm});
            skLineSegment(sketch, "E300", {"start": v(28799.93, -78951.12) * mm, "end": v(29540.7, -79129.76) * mm});
            skLineSegment(sketch, "E301", {"start": v(26511.22, -82266.17) * mm, "end": v(26296.86, -83155.09) * mm});
            skLineSegment(sketch, "E302", {"start": v(26296.86, -83155.09) * mm, "end": v(28222.85, -83619.53) * mm});
            skLineSegment(sketch, "E303", {"start": v(28222.85, -83619.53) * mm, "end": v(28437.2, -82730.61) * mm});
            skLineSegment(sketch, "E304", {"start": v(28437.2, -82730.61) * mm, "end": v(26511.22, -82266.17) * mm});
            skLineSegment(sketch, "E305", {"start": v(27492.99, -78844.99) * mm, "end": v(29418.98, -79309.43) * mm});
            skLineSegment(sketch, "E306", {"start": v(29418.98, -79309.43) * mm, "end": v(29204.62, -80198.35) * mm});
            skLineSegment(sketch, "E307", {"start": v(29204.62, -80198.35) * mm, "end": v(27278.63, -79733.9) * mm});
            skLineSegment(sketch, "E308", {"start": v(27278.63, -79733.9) * mm, "end": v(27492.99, -78844.99) * mm});
            skLineSegment(sketch, "E309", {"start": v(25456.74, -80300.5) * mm, "end": v(25567.85, -80327.29) * mm});
            skLineSegment(sketch, "E310", {"start": v(25671.1, -79411.58) * mm, "end": v(25782.21, -79438.37) * mm});
            skLineSegment(sketch, "E311", {"start": v(25885.45, -78522.66) * mm, "end": v(25996.57, -78549.45) * mm});
            skLineSegment(sketch, "E312", {"start": v(25941.01, -78536.05) * mm, "end": v(25726.65, -79424.97) * mm});
            skLineSegment(sketch, "E313", {"start": v(25726.65, -79424.97) * mm, "end": v(25512.3, -80313.9) * mm});
            skSolve(sketch);
        }
        {
            var Q0;
            Q0=makeQuery(id+"F8.imprint","IMPRINT",FACE,{"disambiguationData":[TD([[makeQuery(id+"F8.imprint","IMPRINT",EDGE,{"derivedFrom":sQuery(id+"F8.wireOp",EDGE,"E27")}),1.0]])]});
            var Q1;
            {var subQ11=sQuery(id+"F8.wireOp",EDGE,"E50");Q1=makeQuery(id+"F8.imprint","IMPRINT",FACE,{"disambiguationData":[TD([[makeQuery(id+"F8.imprint","IMPRINT",EDGE,{"derivedFrom":subQ11}),-1.0]])]});}
            var Q2;
            {var subQ0=sQuery(id+"F8.wireOp",EDGE,"E65");Q2=makeQuery(id+"F8.imprint","IMPRINT",FACE,{"disambiguationData":[TD([[makeQuery(id+"F8.imprint","IMPRINT",EDGE,{"derivedFrom":subQ0}),-1.0]])]});}
            var Q3;
            {var subQ4=sQuery(id+"F8.wireOp",EDGE,"rclvcfd8-MIHF-olu5-eLjo-lo3ld7nkITQP");var subQ5=sQuery(id+"F8.wireOp",EDGE,"E61");var subQ6=makeQuery(id+"F8.imprint","INTERSECT",VERTEX,{"derivedFrom":[subQ5,subQ4]});Q3=makeQuery(id+"F8.imprint","IMPRINT",FACE,{"disambiguationData":[TD([[makeQuery(id+"F8.imprint","IMPRINT",EDGE,{"disambiguationData":[TD([[subQ6,-1.0]])],"derivedFrom":subQ5}),-1.0]])]});}
            var Q4;
            {var subQ0=sQuery(id+"F8.wireOp",EDGE,"E120");Q4=makeQuery(id+"F8.imprint","IMPRINT",FACE,{"disambiguationData":[TD([[makeQuery(id+"F8.imprint","IMPRINT",EDGE,{"derivedFrom":subQ0}),-1.0]])]});}
            var Q5;
            {var subQ0=sQuery(id+"F8.wireOp",EDGE,"E179");Q5=makeQuery(id+"F8.imprint","IMPRINT",FACE,{"disambiguationData":[TD([[makeQuery(id+"F8.imprint","IMPRINT",EDGE,{"derivedFrom":subQ0}),1.0]])]});}
            var Q6;
            {var subQ1=sQuery(id+"F8.wireOp",EDGE,"E104");Q6=makeQuery(id+"F8.imprint","IMPRINT",FACE,{"disambiguationData":[TD([[makeQuery(id+"F8.imprint","IMPRINT",EDGE,{"derivedFrom":subQ1}),-1.0]])]});}
            var Q7;
            {var subQ0=sQuery(id+"F8.wireOp",EDGE,"E176");Q7=makeQuery(id+"F8.imprint","IMPRINT",FACE,{"disambiguationData":[TD([[makeQuery(id+"F8.imprint","IMPRINT",EDGE,{"derivedFrom":subQ0}),-1.0]])]});}
            var Q8;
            {var subQ9=sQuery(id+"F8.wireOp",EDGE,"E117");Q8=makeQuery(id+"F8.imprint","IMPRINT",FACE,{"disambiguationData":[TD([[makeQuery(id+"F8.imprint","IMPRINT",EDGE,{"derivedFrom":subQ9}),1.0]])]});}
            var Q9;
            {var subQ5=sQuery(id+"F8.wireOp",EDGE,"GEOfW8i7-v1bV-P7JK-g7ps-RluW9onRIqib");Q9=makeQuery(id+"F8.imprint","IMPRINT",FACE,{"disambiguationData":[TD([[makeQuery(id+"F8.imprint","IMPRINT",EDGE,{"derivedFrom":subQ5}),1.0]])]});}
            var Q10;
            {var subQ0=sQuery(id+"F8.wireOp",EDGE,"E123");var subQ1=sQuery(id+"F8.wireOp",EDGE,"E118");var subQ2=makeQuery(id+"F8.imprint","INTERSECT",VERTEX,{"derivedFrom":[subQ1,subQ0]});Q10=makeQuery(id+"F8.imprint","IMPRINT",FACE,{"disambiguationData":[TD([[makeQuery(id+"F8.imprint","IMPRINT",EDGE,{"disambiguationData":[TD([[subQ2,1.0]])],"derivedFrom":subQ1}),1.0]])]});}
            var Q11;
            {var subQ0=sQuery(id+"F8.wireOp",EDGE,"E123");var subQ5=sQuery(id+"F8.wireOp",EDGE,"DJspllXv-pb2S-FSFw-zfOf-plQMQFauy2Zp");var subQ10=makeQuery(id+"F8.imprint","INTERSECT",VERTEX,{"derivedFrom":[subQ5,subQ0]});Q11=makeQuery(id+"F8.imprint","IMPRINT",FACE,{"disambiguationData":[TD([[makeQuery(id+"F8.imprint","IMPRINT",EDGE,{"disambiguationData":[TD([[subQ10,-1.0]])],"derivedFrom":subQ5}),1.0]])]});}
            var Q12;
            {var subQ0=sQuery(id+"F8.wireOp",EDGE,"E127");var subQ1=sQuery(id+"F8.wireOp",EDGE,"E124");var subQ2=makeQuery(id+"F8.imprint","INTERSECT",VERTEX,{"derivedFrom":[subQ1,subQ0]});Q12=makeQuery(id+"F8.imprint","IMPRINT",FACE,{"disambiguationData":[TD([[makeQuery(id+"F8.imprint","IMPRINT",EDGE,{"disambiguationData":[TD([[subQ2,-1.0]])],"derivedFrom":subQ1}),-1.0]])]});}
            var Q13;
            {var subQ0=sQuery(id+"F8.wireOp",EDGE,"E125");var subQ1=sQuery(id+"F8.wireOp",EDGE,"E124");var subQ2=makeQuery(id+"F8.imprint","INTERSECT",VERTEX,{"derivedFrom":[subQ1,subQ0]});Q13=makeQuery(id+"F8.imprint","IMPRINT",FACE,{"disambiguationData":[TD([[makeQuery(id+"F8.imprint","IMPRINT",EDGE,{"disambiguationData":[TD([[subQ2,1.0]])],"derivedFrom":subQ1}),-1.0]])]});}
            var Q14;
            {var subQ1=sQuery(id+"F8.wireOp",EDGE,"E67");var subQ6=sQuery(id+"F8.wireOp",EDGE,"E127");var subQ7=makeQuery(id+"F8.imprint","INTERSECT",VERTEX,{"derivedFrom":[subQ1,subQ6]});Q14=makeQuery(id+"F8.imprint","IMPRINT",FACE,{"disambiguationData":[TD([[makeQuery(id+"F8.imprint","IMPRINT",EDGE,{"disambiguationData":[TD([[subQ7,1.0]])],"derivedFrom":subQ1}),-1.0]])]});}
            var Q15;
            {var subQ4=sQuery(id+"F8.wireOp",EDGE,"E126");var subQ5=sQuery(id+"F8.wireOp",EDGE,"E67");var subQ6=makeQuery(id+"F8.imprint","INTERSECT",VERTEX,{"derivedFrom":[subQ5,subQ4]});Q15=makeQuery(id+"F8.imprint","IMPRINT",FACE,{"disambiguationData":[TD([[makeQuery(id+"F8.imprint","IMPRINT",EDGE,{"disambiguationData":[TD([[subQ6,-1.0]])],"derivedFrom":subQ4}),-1.0]])]});}
            var Q16;
            {var subQ16=sQuery(id+"F8.wireOp",EDGE,"E58.0");Q16=makeQuery(id+"F8.imprint","IMPRINT",FACE,{"disambiguationData":[TD([[makeQuery(id+"F8.imprint","IMPRINT",EDGE,{"derivedFrom":subQ16}),1.0]])]});}
            extrude(context, id + "F9", {"entities" : qUnion([Q0, Q1, Q2, Q3, Q4, Q5, Q6, Q7, Q8, Q9, Q10, Q11, Q12, Q13, Q14, Q15, Q16]), "operationType" : NewBodyOperationType.ADD, "depth" : 3048 * mm, "offsetDistance" : 25.4 * mm});
        }
    });
